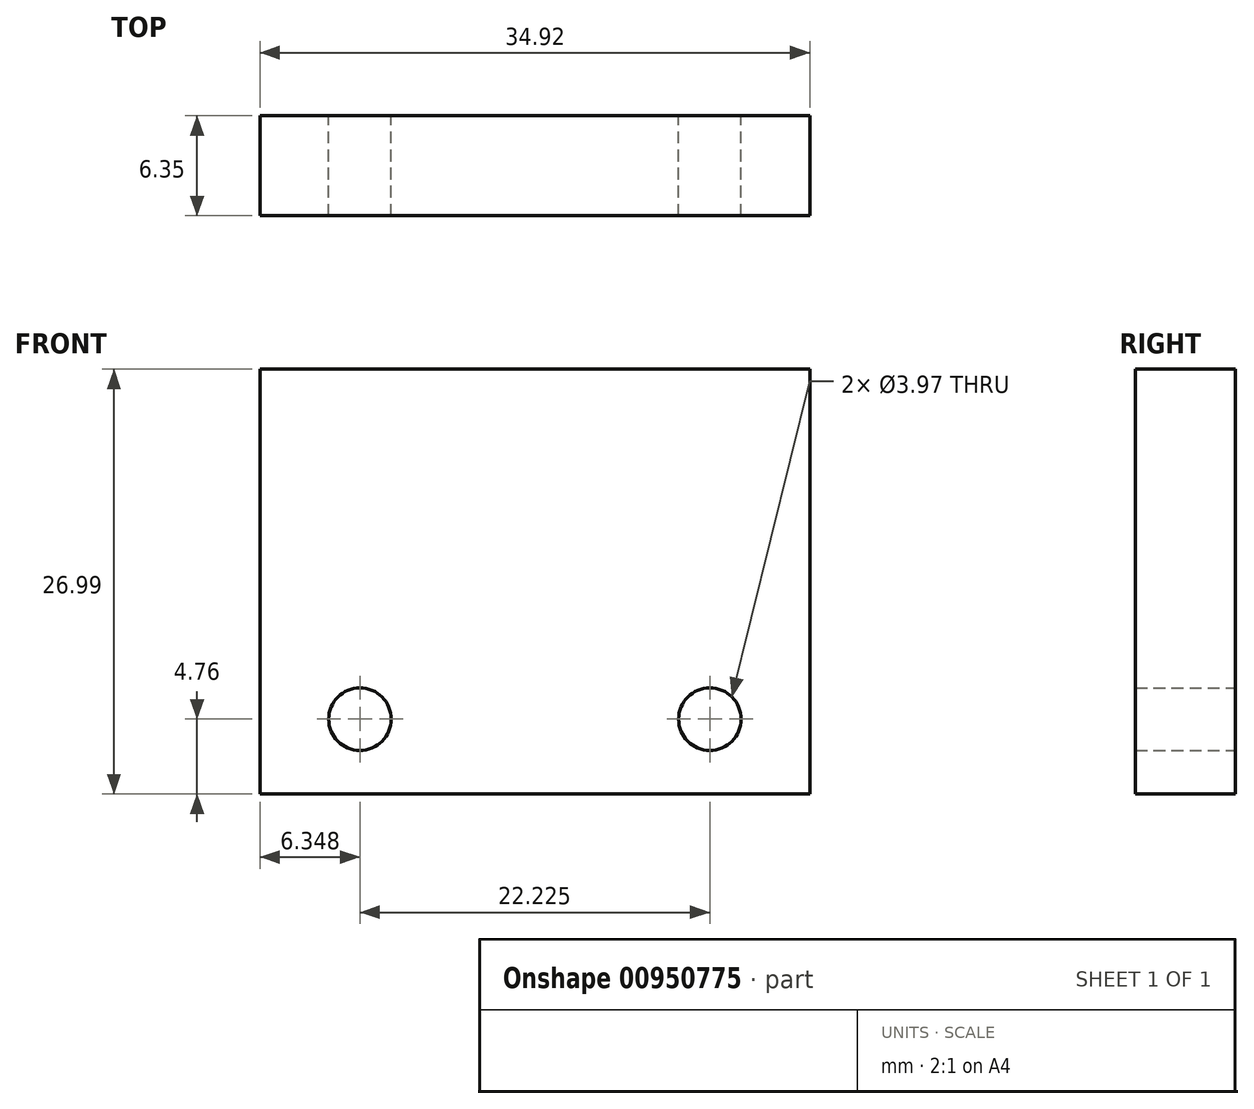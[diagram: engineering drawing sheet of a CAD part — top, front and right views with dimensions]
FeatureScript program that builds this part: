
annotation { "Feature Type Name" : "Feature", "Feature Type Description" : "" }
export const myFeature = defineFeature(function(context is Context, id is Id, definition is map)
    precondition{}
    {
        {
            var Q0;
            Q0=qCreatedBy(makeId("Front.planeOp"),FACE);
            var sketch = newSketch(context, id + "F0", { "sketchPlane" : qUnion([Q0])});
            skLineSegment(sketch, "E0.bottom", {"start": v(-16.5, 21.37) * mm, "end": v(18.43, 21.37) * mm});
            skLineSegment(sketch, "E0.top", {"start": v(-16.5, -5.62) * mm, "end": v(18.43, -5.62) * mm});
            skLineSegment(sketch, "E0.left", {"start": v(-16.5, 21.37) * mm, "end": v(-16.5, -5.62) * mm});
            skLineSegment(sketch, "E0.right", {"start": v(18.43, 21.37) * mm, "end": v(18.43, -5.62) * mm});
            skLineSegment(sketch, "E1", {"start": v(-16.5, -5.62) * mm, "end": v(-10.14, -5.62) * mm});
            skLineSegment(sketch, "E2", {"start": v(-10.14, -5.62) * mm, "end": v(-10.14, -0.86) * mm});
            skLineSegment(sketch, "E3", {"start": v(18.43, -5.62) * mm, "end": v(12.08, -5.62) * mm});
            skLineSegment(sketch, "E4", {"start": v(12.08, -5.62) * mm, "end": v(12.08, -0.86) * mm});
            skLineSegment(sketch, "E5", {"start": v(-16.5, -5.62) * mm, "end": v(-16.5, -4.03) * mm});
            skLineSegment(sketch, "E6", {"start": v(-16.5, -4.03) * mm, "end": v(18.43, -4.03) * mm});
            skCircle(sketch, "E7", {"center": v(-10.14, -0.86) * mm, "radius": 3.18 * mm});
            skCircle(sketch, "E8", {"center": v(12.08, -0.86) * mm, "radius": 3.18 * mm});
            skLineSegment(sketch, "E9", {"start": v(-10.14, -0.86) * mm, "end": v(-10.14, 1.12) * mm});
            skLineSegment(sketch, "E10", {"start": v(12.08, -0.86) * mm, "end": v(12.08, 1.12) * mm});
            skCircle(sketch, "E11", {"center": v(-10.14, -0.86) * mm, "radius": 1.98 * mm});
            skCircle(sketch, "E12", {"center": v(12.08, -0.86) * mm, "radius": 1.98 * mm});
            skSolve(sketch);
        }
        {
            var Q0;
            {var subQ1=sQuery(id+"F0.wireOp",EDGE,"E0.bottom");Q0=makeQuery(id+"F0.imprint","IMPRINT",FACE,{"disambiguationData":[TD([[makeQuery(id+"F0.imprint","IMPRINT",EDGE,{"derivedFrom":subQ1}),-1.0]])]});}
            var Q1;
            {var subQ0=sQuery(id+"F0.wireOp",EDGE,"E1");Q1=makeQuery(id+"F0.imprint","IMPRINT",FACE,{"disambiguationData":[TD([[makeQuery(id+"F0.imprint","IMPRINT",EDGE,{"derivedFrom":subQ0}),1.0]])]});}
            var Q2;
            {var subQ0=sQuery(id+"F0.wireOp",EDGE,"E0.top");Q2=makeQuery(id+"F0.imprint","IMPRINT",FACE,{"disambiguationData":[TD([[makeQuery(id+"F0.imprint","IMPRINT",EDGE,{"derivedFrom":subQ0}),1.0]])]});}
            var Q3;
            {var subQ0=sQuery(id+"F0.wireOp",EDGE,"E3");Q3=makeQuery(id+"F0.imprint","IMPRINT",FACE,{"disambiguationData":[TD([[makeQuery(id+"F0.imprint","IMPRINT",EDGE,{"derivedFrom":subQ0}),-1.0]])]});}
            var Q4;
            Q4=makeQuery(id+"F0.imprint","IMPRINT",FACE,{"disambiguationData":[TD([[makeQuery(id+"F0.imprint","IMPRINT",EDGE,{"derivedFrom":sQuery(id+"F0.wireOp",EDGE,"E8")}),1.0]])]});
            var Q5;
            Q5=makeQuery(id+"F0.imprint","IMPRINT",FACE,{"disambiguationData":[TD([[makeQuery(id+"F0.imprint","IMPRINT",EDGE,{"derivedFrom":sQuery(id+"F0.wireOp",EDGE,"E7")}),1.0]])]});
            extrude(context, id + "F1", {"entities" : qUnion([Q0, Q1, Q2, Q3, Q4, Q5]), "depth" : 6.35 * mm, "offsetDistance" : 25.4 * mm});
        }
    });
